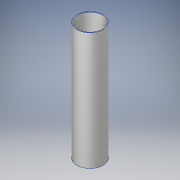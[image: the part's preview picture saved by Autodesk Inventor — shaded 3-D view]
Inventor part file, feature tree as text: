
AUTODESK INVENTOR PART (.ipt)
format: ipt  version: 2017 SP1 (Build 210196100, 196)  size: 98,816 bytes
history: native  units: in
note: dims shown in document units (in); Inventor stores cm internally (conversion verified against a paired STEP export)
features: extrude x1, sketch x1
ambient origin geometry x8: Origin, YZ Plane, XZ Plane, XY Plane, X Axis, Y Axis, Z Axis, Center Point
bodies: Solid1 (feature_tree)
feature tree (2):
  extrude  "Extrusion1"  Depth=36.0in
  sketch  "Sketch1"  dims[d0=8.0in d1=7.5in d2=36.0in d3=0.0in]
